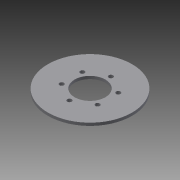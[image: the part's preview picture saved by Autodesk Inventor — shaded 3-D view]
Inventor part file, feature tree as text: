
AUTODESK INVENTOR PART (.ipt)
format: ipt  version: 2013 (Build 170138000, 138)  size: 101,888 bytes
history: native  units: in
note: dims shown in document units (in); Inventor stores cm internally (conversion verified against a paired STEP export)
features: extrude x1, sketch x1
ambient origin geometry x8: Origin, YZ Plane, XZ Plane, XY Plane, X Axis, Y Axis, Z Axis, Center Point
feature tree (2):
  extrude  "Extrusion2"  Depth=6.495in
  sketch  "Sketch1"  dims[d0=1.375in d5=6.495in d16=0.1969in d17=0.1969in d18=60.0deg d19=0.1969in d20=1.6555in d21=0.1969in d22=60.0deg d23=0.1969in d24=0.1969in d25=60.0deg d26=60.0deg d27=0.125in d28=0.0in]
